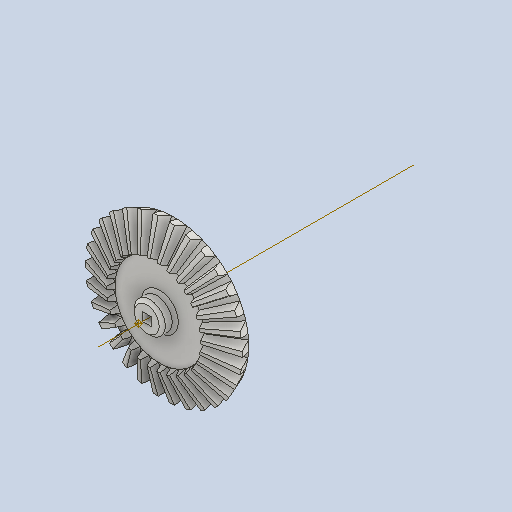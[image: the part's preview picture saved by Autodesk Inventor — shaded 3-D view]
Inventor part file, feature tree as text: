
AUTODESK INVENTOR PART (.ipt)
format: ipt  version: 2022 (Build 260153000, 153)  size: 705,536 bytes
history: native  units: in
note: dims shown in document units (in); Inventor stores cm internally (conversion verified against a paired STEP export)
features: other x30, sketch x3
ambient origin geometry x8: Origin, YZ Plane, XZ Plane, XY Plane, X Axis, Y Axis, Z Axis, Center Point
bodies: Solid1 (feature_tree)
feature tree (33):
  other  "Bevel Gear21_MIR1.ipt"
  other  "Solid1::Bevel Gear21_MIR1.ipt"
  other  "TaggingFeature1"
  other  "Teeth Body Sketch"
  other  "Start Sketch"
  other  "End Sketch"
  other  "End Sketch Right"
  other  "End Sketch Left"
  other  "Body Sketch"
  sketch  "Sketch6"  dims[d0=0.3937in]
  sketch  "Sketch8"  dims[d48=0.0in d49=0.0in d50=90.0deg d52=0.0in d53=0.0in d54=0.0in]
  sketch  "Sketch9"
  other  "3D Sketch Right"
  other  "3D Sketch Left"
  other  "Mesh Plane"
  other  "Top Plane"
  other  "Mesh Plane2"
  other  "Tooth Plane"
  other  "End Plane"
  other  "End Plane Right"
  other  "End Plane Left"
  other  "Z Axis_1"
  other  "Top Point"
  other  "Start Point"
  other  "End Point"
  other  "Srf1"
  other  "Srf1::Derived"
  other  "Start plane iMate"
  other  "Mesh iMate2"
  other  "Axis Angle iMate"
  other  "Axis iMate"
  other  "Mesh iMate"
  other  "Intersection iMate"
